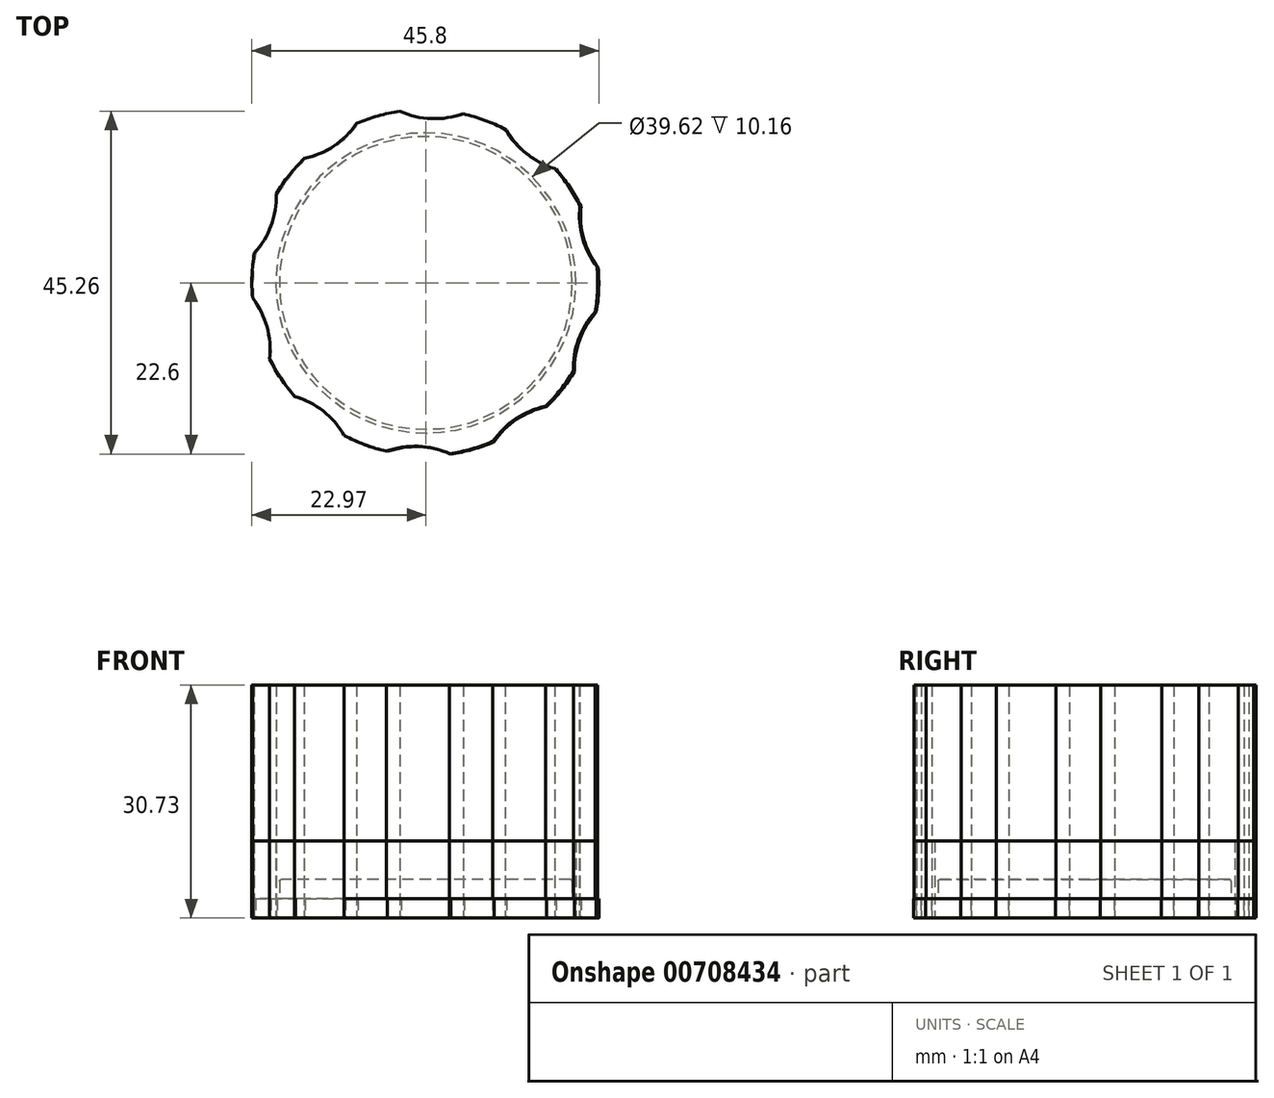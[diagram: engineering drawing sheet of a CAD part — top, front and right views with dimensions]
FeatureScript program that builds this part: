
annotation { "Feature Type Name" : "Feature", "Feature Type Description" : "" }
export const myFeature = defineFeature(function(context is Context, id is Id, definition is map)
    precondition{}
    {
        {
            var Q0;
            Q0=qCreatedBy(makeId("Top.planeOp"),FACE);
            var sketch = newSketch(context, id + "F0", { "sketchPlane" : qUnion([Q0])});
            skCircle(sketch, "E0", {"center": v(0, 0) * mm, "radius": 22.83 * mm});
            skCircle(sketch, "E1", {"center": v(-18.23, 27.33) * mm, "radius": 11.2 * mm});
            skCircle(sketch, "E2.1.0", {"center": v(-30.81, 11.4) * mm, "radius": 11.2 * mm});
            skCircle(sketch, "E2.2.0", {"center": v(-31.62, -8.9) * mm, "radius": 11.2 * mm});
            skCircle(sketch, "E2.3.0", {"center": v(-20.36, -25.78) * mm, "radius": 11.2 * mm});
            skCircle(sketch, "E2.4.0", {"center": v(-1.31, -32.83) * mm, "radius": 11.2 * mm});
            skCircle(sketch, "E2.5.0", {"center": v(18.23, -27.33) * mm, "radius": 11.2 * mm});
            skCircle(sketch, "E2.6.0", {"center": v(30.81, -11.4) * mm, "radius": 11.2 * mm});
            skCircle(sketch, "E2.7.0", {"center": v(31.62, 8.9) * mm, "radius": 11.2 * mm});
            skCircle(sketch, "E2.8.0", {"center": v(20.36, 25.78) * mm, "radius": 11.2 * mm});
            skCircle(sketch, "E2.9.0", {"center": v(1.31, 32.83) * mm, "radius": 11.2 * mm});
            skSolve(sketch);
        }
        {
            var Q0;
            {var subQ0=sQuery(id+"F0.wireOp",EDGE,"E2.7.0");var subQ1=sQuery(id+"F0.wireOp",EDGE,"E0");var subQ5=makeQuery(id+"F0.imprint","INTERSECT",VERTEX,{"disambiguationData":[OD(0.0)],"derivedFrom":[subQ1,subQ0]});Q0=makeQuery(id+"F0.imprint","IMPRINT",FACE,{"disambiguationData":[TD([[makeQuery(id+"F0.imprint","IMPRINT",EDGE,{"disambiguationData":[TD([[subQ5,-1.0]])],"derivedFrom":subQ1}),1.0]])]});}
            extrude(context, id + "F1", {"entities" : qUnion([Q0]), "depth" : 2.54 * mm, "offsetDistance" : 25.4 * mm});
        }
        {
            var Q0;
            Q0=qCreatedBy(makeId("Top.planeOp"),FACE);
            var sketch = newSketch(context, id + "F2", { "sketchPlane" : qUnion([Q0])});
            skCircle(sketch, "E3", {"center": v(0, 0) * mm, "radius": 19.33 * mm});
            skSolve(sketch);
        }
        {
            var Q0;
            Q0 = qSketchRegion(id + "F2", true);
            extrude(context, id + "F3", {"entities" : qUnion([Q0]), "operationType" : NewBodyOperationType.ADD, "depth" : 5.08 * mm, "offsetDistance" : 25.4 * mm});
        }
        {
            var Q0;
            Q0=makeQuery(id+"F3.opExtrude","CAP_FACE",FACE,{"disambiguationData":[OSD([sQuery(id+"F2.wireOp",EDGE,"E3")])],"isStart":false});
            fillet(context, id + "F4", {"entities" : qUnion([Q0]), "radius" : 0.25 * mm, "tangentPropagation" : true, "allowEdgeOverflow" : false});
        }
        {
            var Q0;
            Q0=makeQuery(id+"F1.opExtrude","SWEPT_BODY",BODY,{"disambiguationData":[OSD([sQuery(id+"F0.wireOp",EDGE,"E0"),sQuery(id+"F0.wireOp",EDGE,"E1"),sQuery(id+"F0.wireOp",EDGE,"E2.1.0"),sQuery(id+"F0.wireOp",EDGE,"E2.2.0"),sQuery(id+"F0.wireOp",EDGE,"E2.3.0"),sQuery(id+"F0.wireOp",EDGE,"E2.4.0"),sQuery(id+"F0.wireOp",EDGE,"E2.5.0"),sQuery(id+"F0.wireOp",EDGE,"E2.6.0"),sQuery(id+"F0.wireOp",EDGE,"E2.7.0"),sQuery(id+"F0.wireOp",EDGE,"E2.8.0"),sQuery(id+"F0.wireOp",EDGE,"E2.9.0")])]});
            transform(context, id + "F5", {"entities" : qUnion([Q0]), "transformType" : TransformType.TRANSLATION_3D, "dx" : 0 * mm, "dy" : 0 * mm, "dz" : 0 * mm, "makeCopy" : true});
        }
        {
            var Q0;
            Q0=makeQuery(id+"F5.opPattern","COPY",BODY,{"derivedFrom":makeQuery(id+"F1.opExtrude","SWEPT_BODY",BODY,{"disambiguationData":[OSD([sQuery(id+"F0.wireOp",EDGE,"E0"),sQuery(id+"F0.wireOp",EDGE,"E1"),sQuery(id+"F0.wireOp",EDGE,"E2.1.0"),sQuery(id+"F0.wireOp",EDGE,"E2.2.0"),sQuery(id+"F0.wireOp",EDGE,"E2.3.0"),sQuery(id+"F0.wireOp",EDGE,"E2.4.0"),sQuery(id+"F0.wireOp",EDGE,"E2.5.0"),sQuery(id+"F0.wireOp",EDGE,"E2.6.0"),sQuery(id+"F0.wireOp",EDGE,"E2.7.0"),sQuery(id+"F0.wireOp",EDGE,"E2.8.0"),sQuery(id+"F0.wireOp",EDGE,"E2.9.0")])]}),"instanceName":"1"});
            deleteBodies(context, id + "F6", {"entities" : qUnion([Q0])});
        }
        {
            var Q0;
            Q0=makeQuery(id+"F1.opExtrude","SWEPT_BODY",BODY,{"disambiguationData":[OSD([sQuery(id+"F0.wireOp",EDGE,"E0"),sQuery(id+"F0.wireOp",EDGE,"E1"),sQuery(id+"F0.wireOp",EDGE,"E2.1.0"),sQuery(id+"F0.wireOp",EDGE,"E2.2.0"),sQuery(id+"F0.wireOp",EDGE,"E2.3.0"),sQuery(id+"F0.wireOp",EDGE,"E2.4.0"),sQuery(id+"F0.wireOp",EDGE,"E2.5.0"),sQuery(id+"F0.wireOp",EDGE,"E2.6.0"),sQuery(id+"F0.wireOp",EDGE,"E2.7.0"),sQuery(id+"F0.wireOp",EDGE,"E2.8.0"),sQuery(id+"F0.wireOp",EDGE,"E2.9.0")])]});
            transform(context, id + "F7", {"entities" : qUnion([Q0]), "transformType" : TransformType.TRANSLATION_3D, "dx" : 0 * mm, "dy" : 0 * mm, "dz" : 6.35 * mm, "makeCopy" : true});
        }
        {
            var Q0;
            Q0=makeQuery(id+"F7.opPattern","COPY",BODY,{"derivedFrom":makeQuery(id+"F1.opExtrude","SWEPT_BODY",BODY,{"disambiguationData":[OSD([sQuery(id+"F0.wireOp",EDGE,"E0"),sQuery(id+"F0.wireOp",EDGE,"E1"),sQuery(id+"F0.wireOp",EDGE,"E2.1.0"),sQuery(id+"F0.wireOp",EDGE,"E2.2.0"),sQuery(id+"F0.wireOp",EDGE,"E2.3.0"),sQuery(id+"F0.wireOp",EDGE,"E2.4.0"),sQuery(id+"F0.wireOp",EDGE,"E2.5.0"),sQuery(id+"F0.wireOp",EDGE,"E2.6.0"),sQuery(id+"F0.wireOp",EDGE,"E2.7.0"),sQuery(id+"F0.wireOp",EDGE,"E2.8.0"),sQuery(id+"F0.wireOp",EDGE,"E2.9.0")])]}),"instanceName":"1"});
            deleteBodies(context, id + "F8", {"entities" : qUnion([Q0])});
        }
        {
            var Q0;
            Q0=qCreatedBy(makeId("Top.planeOp"),FACE);
            var sketch = newSketch(context, id + "F9", { "sketchPlane" : qUnion([Q0])});
            skCircle(sketch, "E4", {"center": v(-0.14, 0.06) * mm, "radius": 22.83 * mm});
            skCircle(sketch, "E5", {"center": v(-18.37, 27.4) * mm, "radius": 11.2 * mm});
            skCircle(sketch, "E6.1.0", {"center": v(-30.95, 11.45) * mm, "radius": 11.2 * mm});
            skCircle(sketch, "E6.2.0", {"center": v(-31.77, -8.83) * mm, "radius": 11.2 * mm});
            skCircle(sketch, "E6.3.0", {"center": v(-20.5, -25.72) * mm, "radius": 11.2 * mm});
            skCircle(sketch, "E6.4.0", {"center": v(-1.45, -32.76) * mm, "radius": 11.2 * mm});
            skCircle(sketch, "E6.5.0", {"center": v(18.1, -27.26) * mm, "radius": 11.2 * mm});
            skCircle(sketch, "E6.6.0", {"center": v(30.67, -11.33) * mm, "radius": 11.2 * mm});
            skCircle(sketch, "E6.7.0", {"center": v(31.48, 8.96) * mm, "radius": 11.2 * mm});
            skCircle(sketch, "E6.8.0", {"center": v(20.21, 25.85) * mm, "radius": 11.2 * mm});
            skCircle(sketch, "E6.9.0", {"center": v(1.17, 32.89) * mm, "radius": 11.2 * mm});
            skCircle(sketch, "E7", {"center": v(0, 0) * mm, "radius": 19.81 * mm});
            skSolve(sketch);
        }
        {
            var Q0;
            Q0=makeQuery(id+"F9.imprint","IMPRINT",FACE,{"disambiguationData":[TD([[makeQuery(id+"F9.imprint","IMPRINT",EDGE,{"derivedFrom":sQuery(id+"F9.wireOp",EDGE,"E7")}),-1.0]])]});
            extrude(context, id + "F10", {"entities" : qUnion([Q0]), "depth" : 10.16 * mm, "offsetDistance" : 25.4 * mm});
        }
        {
            var Q0;
            Q0=makeQuery(id+"F9.imprint","IMPRINT",FACE,{"disambiguationData":[TD([[makeQuery(id+"F9.imprint","IMPRINT",EDGE,{"derivedFrom":sQuery(id+"F9.wireOp",EDGE,"E7")}),-1.0]])]});
            var sketch = newSketch(context, id + "F11", { "sketchPlane" : qUnion([Q0])});
            skSolve(sketch);
        }
        {
            var Q0;
            Q0=makeQuery(id+"F11.imprint","IMPRINT",FACE,{"disambiguationData":[TD([[makeQuery(id+"F11.imprint","IMPRINT",EDGE,{"derivedFrom":makeQuery(id+"F9.imprint","IMPRINT",EDGE,{"derivedFrom":sQuery(id+"F9.wireOp",EDGE,"E7")})}),-1.0]])]});
            var Q1;
            Q1=makeQuery(id+"F11.imprint","IMPRINT",FACE,{"disambiguationData":[TD([[makeQuery(id+"F11.imprint","IMPRINT",EDGE,{"derivedFrom":makeQuery(id+"F9.imprint","IMPRINT",EDGE,{"derivedFrom":sQuery(id+"F9.wireOp",EDGE,"E7")})}),1.0]])]});
            extrude(context, id + "F12", {"entities" : qUnion([Q0, Q1]), "depth" : 30.73 * mm, "offsetDistance" : 25.4 * mm});
        }
    });
